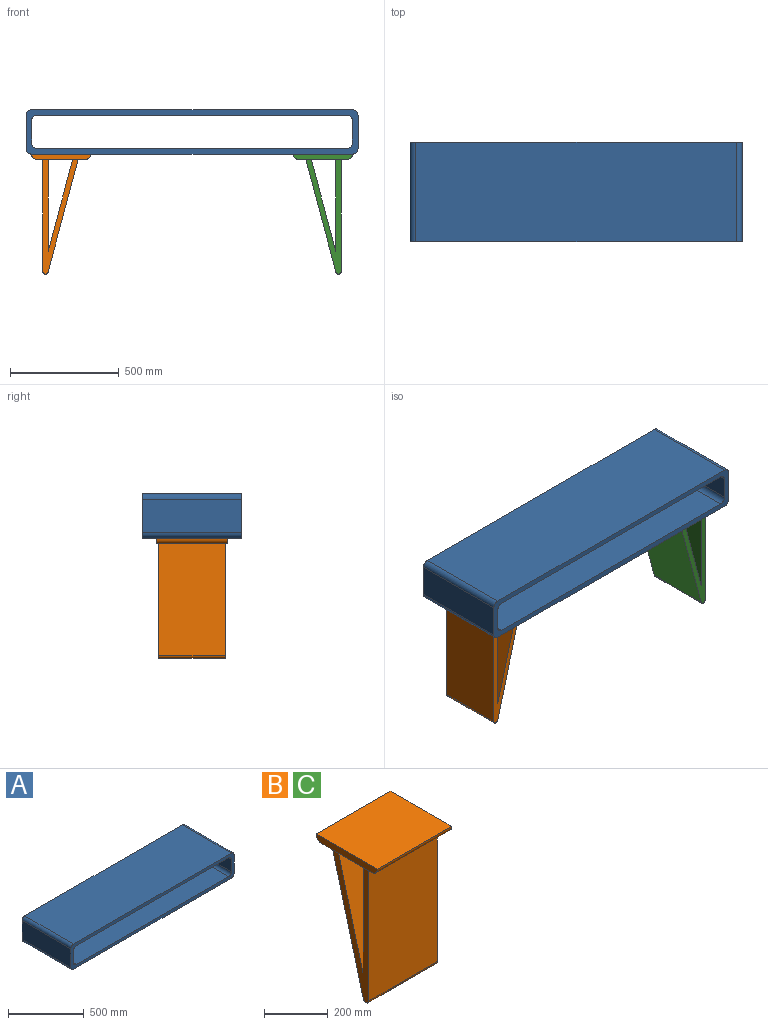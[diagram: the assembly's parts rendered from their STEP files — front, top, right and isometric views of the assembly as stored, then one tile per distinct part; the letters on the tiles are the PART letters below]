
ASSEMBLY  parts=3 mates=2
PART A: 18 faces, bbox 1524x457.2x203.2 mm
  f0: plane 1524x203.2mm, normal (0,1,0), area 85161.1mm2, adj f2,f3,f4,f5,f6,f7,f8,f9
  f1: plane 1524x203.2mm, normal (0,-1,0), area 85161.1mm2, adj f2,f3,f4,f5,f6,f7,f8,f9
  f2: plane 457.2x152.4mm, normal (-1,0,0), area 69677.3mm2, adj f0,f1,f6,f7
  f3: plane 457.2x152.4mm, normal (1,0,0), area 69677.3mm2, adj f0,f1,f8,f9
  f4: plane 1473.2x457.2mm, normal (0,0,1), area 673547mm2, adj f0,f1,f6,f9
  f5: plane 1473.2x457.2mm, normal (0,0,-1), area 673547mm2, adj f0,f1,f7,f8
  f6: cylinder r=25.4mm len=457.2mm, axis (0,1,0), area 18241.5mm2, adj f0,f1,f2,f4
  f7: cylinder r=25.4mm len=457.2mm, axis (0,-1,0), area 18241.5mm2, adj f0,f1,f2,f5
  f8: cylinder r=25.4mm len=457.2mm, axis (0,1,0), area 18241.5mm2, adj f0,f1,f3,f5
  f9: cylinder r=25.4mm len=457.2mm, axis (0,-1,0), area 18241.5mm2, adj f0,f1,f3,f4
  f10: plane 1422.4x457.2mm, normal (0,0,-1), area 650321.3mm2, adj f0,f1,f14,f17
  f11: plane 457.2x101.6mm, normal (1,0,0), area 46451.5mm2, adj f0,f1,f16,f17
  f12: plane 1422.4x457.2mm, normal (0,0,1), area 650321.3mm2, adj f0,f1,f15,f16
  f13: plane 457.2x101.6mm, normal (-1,0,0), area 46451.5mm2, adj f0,f1,f14,f15
  f14: cylinder r=25.4mm len=457.2mm, axis (0,1,0), area 18241.5mm2, adj f0,f1,f10,f13
  f15: cylinder r=25.4mm len=457.2mm, axis (0,-1,0), area 18241.5mm2, adj f0,f1,f12,f13
  f16: cylinder r=25.4mm len=457.2mm, axis (0,1,0), area 18241.5mm2, adj f0,f1,f11,f12
  f17: cylinder r=25.4mm len=457.2mm, axis (0,-1,0), area 18241.5mm2, adj f0,f1,f10,f11
PART B: 13 faces, bbox 330.2x271.7x551.2 mm
  f0: plane 421.95x304.8mm, normal (0,1,0), area 128611.4mm2, adj f3,f4,f5,f9
  f1: plane 513.13x304.8mm, normal (0,-1,0), area 156403.2mm2, adj f4,f5,f6,f9
  f2: plane 516.42x304.8mm, normal (0,0.97,-0.26), area 162957.7mm2, adj f4,f5,f6,f9
  f3: plane 421.95x304.8mm, normal (0,-0.97,0.26), area 133109.6mm2, adj f0,f4,f5,f9
  f4: plane 525.83x163.34mm, normal (1,0,0), area 25043.8mm2, adj f0,f1,f2,f3,f6,f9
  f5: plane 525.83x163.34mm, normal (-1,0,0), area 25043.8mm2, adj f0,f1,f2,f3,f6,f9
  f6: cylinder r=12.7mm len=304.8mm, axis (-1,0,0), area 11147.6mm2, adj f1,f2,f4,f5
  f7: plane 271.75x25.4mm, normal (1,0,0), area 6625.5mm2, adj f9,f10,f11,f12
  f8: plane 271.75x25.4mm, normal (-1,0,0), area 6625.5mm2, adj f9,f10,f11,f12
  f9: plane 330.2x220.95mm, normal (0,0,-1), area 57482.1mm2, adj f0,f1,f2,f3,f4,f5,f7,f8
  f10: plane 330.2x271.75mm, normal (0,0,1), area 89731.1mm2, adj f7,f8,f11,f12
  f11: cylinder r=25.4mm len=330.2mm, axis (1,0,0), area 13174.4mm2, adj f7,f8,f9,f10
  f12: cylinder r=25.4mm len=330.2mm, axis (-1,0,0), area 13174.4mm2, adj f7,f8,f9,f10
PART C: same geometry as B
PLACE A t=(-124.36,581.62,832.57)mm
PLACE B rot(axis=(0,0,-1),90deg) t=(-577.38,709.02,832.57)mm
PLACE C rot(axis=(0,0,1),90deg) t=(328.66,404.22,832.57)mm
MATE fastened B.f10 <-> A.f5  axis (0,0,1) through (-860.96,556.62,832.57)mm
MATE fastened C.f10 <-> A.f5  axis (0,0,1) through (612.24,556.62,832.57)mm
